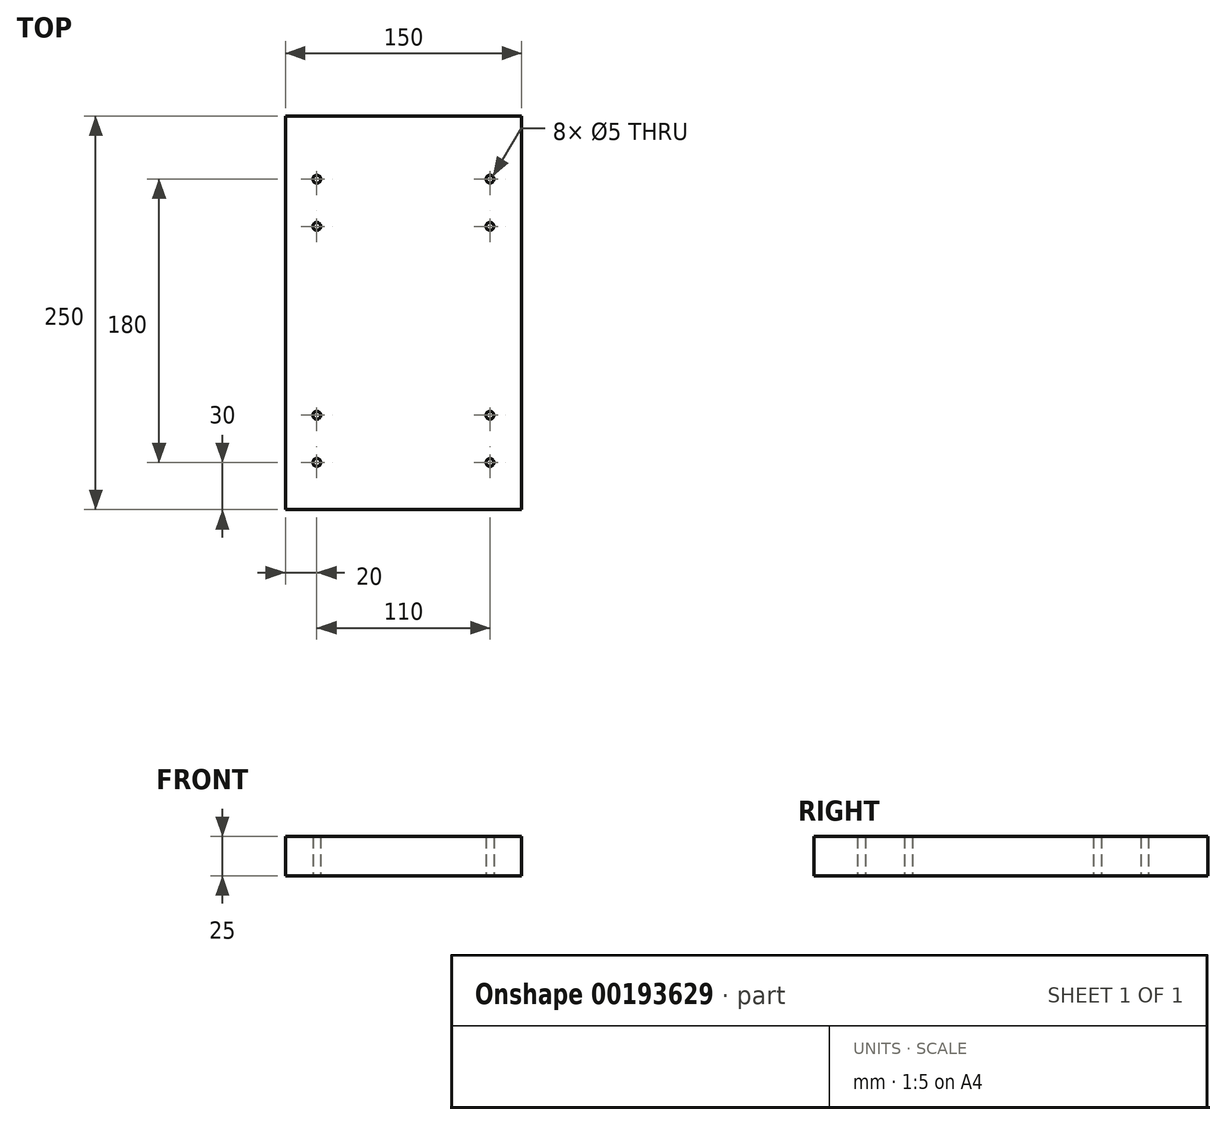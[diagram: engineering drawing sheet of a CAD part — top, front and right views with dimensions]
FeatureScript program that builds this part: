
annotation { "Feature Type Name" : "Feature", "Feature Type Description" : "" }
export const myFeature = defineFeature(function(context is Context, id is Id, definition is map)
    precondition{}
    {
        {
            var Q0;
            Q0=qCreatedBy(makeId("Top.planeOp"),FACE);
            var sketch = newSketch(context, id + "F0", { "sketchPlane" : qUnion([Q0])});
            skLineSegment(sketch, "E0.bottom", {"start": v(75, -125) * mm, "end": v(-75, -125) * mm});
            skLineSegment(sketch, "E0.top", {"start": v(75, 125) * mm, "end": v(-75, 125) * mm});
            skLineSegment(sketch, "E0.left", {"start": v(75, -125) * mm, "end": v(75, 125) * mm});
            skLineSegment(sketch, "E0.right", {"start": v(-75, -125) * mm, "end": v(-75, 125) * mm});
            skPoint(sketch, "E0.middle", {"position": v(0, 0) * mm});
            skCircle(sketch, "E1", {"center": v(-55, -95) * mm, "radius": 2.5 * mm});
            skCircle(sketch, "E2", {"center": v(-55, -65) * mm, "radius": 2.5 * mm});
            skCircle(sketch, "E3", {"center": v(-55, 55) * mm, "radius": 2.5 * mm});
            skCircle(sketch, "E4", {"center": v(-55, 85) * mm, "radius": 2.5 * mm});
            skCircle(sketch, "E5", {"center": v(55, -95) * mm, "radius": 2.5 * mm});
            skCircle(sketch, "E6", {"center": v(55, -65) * mm, "radius": 2.5 * mm});
            skCircle(sketch, "E7", {"center": v(55, 55) * mm, "radius": 2.5 * mm});
            skCircle(sketch, "E8", {"center": v(55, 85) * mm, "radius": 2.5 * mm});
            skSolve(sketch);
        }
        {
            var Q0;
            Q0=makeQuery(id+"F0.imprint","IMPRINT",FACE,{"disambiguationData":[TD([[makeQuery(id+"F0.imprint","IMPRINT",EDGE,{"derivedFrom":sQuery(id+"F0.wireOp",EDGE,"E0.bottom")}),-1.0]])]});
            extrude(context, id + "F1", {"entities" : qUnion([Q0]), "depth" : 25 * mm});
        }
    });
